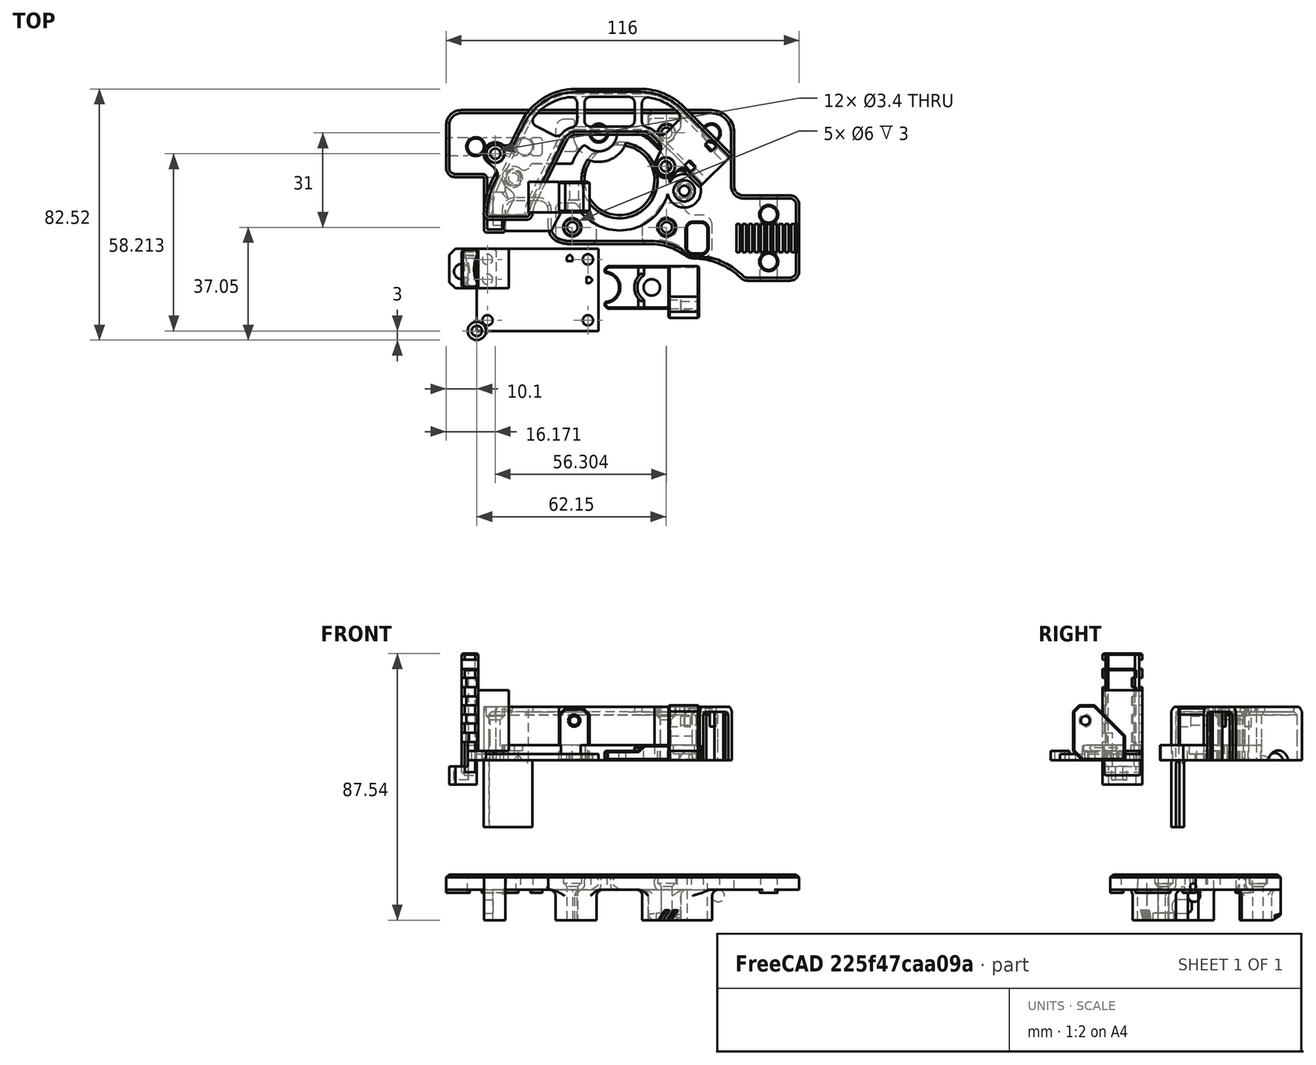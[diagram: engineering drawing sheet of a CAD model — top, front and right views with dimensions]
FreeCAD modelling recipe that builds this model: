
FCSTD DOCUMENT  (FreeCAD 0.19R24291 (Git))
Label: toolhead-pcb-mounter
License: Other
LicenseURL: GPL3
objects: Part::Cylinder×26, Part::Cut×26, Part::Box×24, Part::Chamfer×17, Part::MultiFuse×16, Part::Feature×10, Part::Fillet×6, Part::Extrusion×2, Part::MultiCommon×1
note: 128 computed .brp shape members not serialized (recipe doc carries the construction recipe); baked Part::Feature solids carry a one-line shape summary decoded from their .brp

FEATURE [Part::Box] Box  label="Cube"
  AttacherType = Attacher::AttachEngine3D
  Height = 2
  Length = 40
  Width = 27
FEATURE [Part::Cylinder] Cylinder
  Angle = 360
  AttacherType = Attacher::AttachEngine3D
  Height = 10
  Placement = pos=(3.5,3.5,0) rot=(0,0,1;0rad)
  Radius = 1.7
FEATURE [Part::Cylinder] Cylinder001
  Angle = 360
  AttacherType = Attacher::AttachEngine3D
  Height = 10
  Placement = pos=(3.5,23.5,0) rot=(0,0,1;0rad)
  Radius = 1.7
FEATURE [Part::Cylinder] Cylinder002
  Angle = 360
  AttacherType = Attacher::AttachEngine3D
  Height = 10
  Placement = pos=(36.5,3.5,0) rot=(0,0,1;0rad)
  Radius = 1.7
FEATURE [Part::Cylinder] Cylinder003
  Angle = 360
  AttacherType = Attacher::AttachEngine3D
  Height = 10
  Placement = pos=(36.5,23.5,0) rot=(0,0,1;0rad)
  Radius = 1.7
FEATURE [Part::Cylinder] Cylinder004
  Angle = 360
  AttacherType = Attacher::AttachEngine3D
  Height = 10
  Placement = pos=(3.5,17,0) rot=(0,0,1;0rad)
  Radius = 1.7
FEATURE [Part::MultiFuse] Fusion
  Shapes = -> [Cylinder004,Cylinder,Cylinder001,Cylinder002,Cylinder003]
FEATURE [Part::Cut] Cut
  Base = -> Box
  Tool = -> Fusion
FEATURE [Part::Box] Box001  label="Cube001"
  AttacherType = Attacher::AttachEngine3D
  Height = 10
  Length = 2
  Placement = pos=(29.5,23,0) rot=(0,0,1;0rad)
  Width = 2
FEATURE [Part::Box] Box002  label="Cube002"
  AttacherType = Attacher::AttachEngine3D
  Height = 10
  Length = 2
  Placement = pos=(36,15.7,0) rot=(0,0,1;0rad)
  Width = 2
FEATURE [Part::Chamfer] Chamfer
  Base = -> Box002
  Edges = 2 edges r=0.9: [Edge5,Edge7]
FEATURE [Part::Chamfer] Chamfer001
  Base = -> Box001
  Edges = 2 edges r=0.8: [Edge3,Edge7]
FEATURE [Part::MultiFuse] Fusion001
  Shapes = -> [Chamfer,Chamfer001]
FEATURE [Part::Cut] Cut001  label="pcb"
  Base = -> Cut
  Tool = -> Fusion001
FEATURE [Part::Cylinder] Cylinder005
  Angle = 360
  AttacherType = Attacher::AttachEngine3D
  Height = 3
  Radius = 3
FEATURE [Part::Cylinder] Cylinder006
  Angle = 360
  AttacherType = Attacher::AttachEngine3D
  Height = 3
  Radius = 1.7
FEATURE [Part::Cylinder] Cylinder007
  Angle = 360
  AttacherType = Attacher::AttachEngine3D
  Height = 10
  Radius = 4.75
FEATURE [Part::Cylinder] Cylinder008
  Angle = 360
  AttacherType = Attacher::AttachEngine3D
  Height = 10
  Placement = pos=(15.5,0,0) rot=(0,0,1;0rad)
  Radius = 2.7
FEATURE [Part::Box] Box003  label="Cube003"
  AttacherType = Attacher::AttachEngine3D
  Height = 5
  Length = 22
  Placement = pos=(0,-7,0) rot=(0,0,1;0rad)
  Width = 14
FEATURE [Part::Cut] Cut003
  Base = -> Box003
  Tool = -> Cylinder007
FEATURE [Part::Box] Box004  label="Cube004"
  AttacherType = Attacher::AttachEngine3D
  Height = 18
  Length = 10
  Placement = pos=(21,-10,0) rot=(0,0,1;0rad)
  Width = 17
FEATURE [Part::Cylinder] Cylinder009
  Angle = 360
  AttacherType = Attacher::AttachEngine3D
  Height = 5
  Placement = pos=(15.5,0,0) rot=(0,0,1;0rad)
  Radius = 5.75
FEATURE [Part::Chamfer] Chamfer002
  Base = -> Cut003
  Edges = 2 edges r=1: [Edge4,Edge20]
FEATURE [Part::Box] Box005  label="Cube005"
  AttacherType = Attacher::AttachEngine3D
  Height = 10
  Length = 18
  Placement = pos=(-24,-7,3) rot=(0,0,1;0rad)
  Width = 14
FEATURE [Part::Chamfer] Chamfer006
  Base = -> Box005
  Edges = 1 edges r=2: [Edge8]
  Placement = pos=(19,0,0) rot=(0,0,1;0rad)
FEATURE [Part::Cut] Cut004
  Base = -> Chamfer002
  Tool = -> Chamfer006
FEATURE [Part::Chamfer] Chamfer008
  Base = -> Cut004
  Edges = 21 edges r=0.4: [Edge1,Edge2,Edge3,Edge5,Edge7,Edge8,Edge9,Edge10,Edge11,Edge12,Edge15,Edge16,Edge17,Edge19,Edge20,Edge21,Edge24,Edge25,Edge27,Edge30,Edge31]
FEATURE [Part::Cylinder] Cylinder010
  Angle = 360
  AttacherType = Attacher::AttachEngine3D
  Height = 4
  Placement = pos=(21,0,18) rot=(0,1,0;1.5708rad)
  Radius = 2
FEATURE [Part::Chamfer] Chamfer001002004
  Base = -> Cylinder009
  Edges = 1 edges r=1: [Edge1]
FEATURE [Part::MultiFuse] Fusion002
  Shapes = -> [Chamfer001002004,Chamfer008]
FEATURE [Part::Cut] Cut005
  Base = -> Fusion002
  Tool = -> Cylinder008
FEATURE [Part::Cylinder] Cylinder011
  Angle = 360
  AttacherType = Attacher::AttachEngine3D
  Height = 13
  Placement = pos=(21,0,18) rot=(0,1,0;1.5708rad)
  Radius = 1.45
FEATURE [Part::Cylinder] Cylinder012
  Angle = 360
  AttacherType = Attacher::AttachEngine3D
  Height = 10
  Placement = pos=(3.5,17,0) rot=(0,0,1;0rad)
  Radius = 1.65
FEATURE [Part::Cylinder] Cylinder013
  Angle = 360
  AttacherType = Attacher::AttachEngine3D
  Height = 10
  Placement = pos=(3.5,23.5,0) rot=(0,0,1;0rad)
  Radius = 1.65
FEATURE [Part::Box] Box006  label="Cube006"
  AttacherType = Attacher::AttachEngine3D
  Height = 3
  Length = 6.5
  Placement = pos=(0,14,0) rot=(0,0,1;0rad)
  Width = 13
FEATURE [Part::Box] Box007  label="Cube007"
  AttacherType = Attacher::AttachEngine3D
  Height = 35
  Length = 7
  Placement = pos=(-5,14,-5) rot=(0,0,1;0rad)
  Width = 13
FEATURE [Part::Cylinder] Cylinder014
  Angle = 360
  AttacherType = Attacher::AttachEngine3D
  Height = 48
  Placement = pos=(-12.75,19.5,-6) rot=(0,0,1;0rad)
  Radius = 10
FEATURE [Part::Box] Box008  label="Cube008"
  AttacherType = Attacher::AttachEngine3D
  Height = 10
  Length = 10
  Placement = pos=(0,14,-10) rot=(0,0,1;0rad)
  Width = 13
FEATURE [Part::Box] Box009  label="Cube009"
  AttacherType = Attacher::AttachEngine3D
  Height = 20
  Length = 10
  Placement = pos=(0.5,14,3) rot=(0,0,1;0rad)
  Width = 13
FEATURE [Part::Box] Box010  label="Cube010"
  AttacherType = Attacher::AttachEngine3D
  Height = 43
  Length = 10
  Placement = pos=(0.5,14,-8) rot=(0,0,1;0rad)
  Width = 13
FEATURE [Part::Box] Box011  label="Cube011"
  AttacherType = Attacher::AttachEngine3D
  Height = 3
  Length = 10
  Placement = pos=(-6,13,6) rot=(0,0,1;0rad)
  Width = 2
FEATURE [Part::Box] Box012  label="Cube012"
  AttacherType = Attacher::AttachEngine3D
  Height = 3
  Length = 10
  Placement = pos=(-6,26,6) rot=(0,0,1;0rad)
  Width = 2
FEATURE [Part::MultiFuse] Fusion007
  Shapes = -> [Box011,Box012]
FEATURE [Part::Feature] Fusion007001  label="Fusion008"
  Placement = pos=(0,0,6) rot=(0,0,1;0rad)
  shape: bbox 10 x 15 x 3 mm, 12 faces, 2 solids (baked)
FEATURE [Part::Feature] Fusion007002  label="Fusion009"
  Placement = pos=(0,0,12) rot=(0,0,1;0rad)
  shape: bbox 10 x 15 x 3 mm, 12 faces, 2 solids (baked)
FEATURE [Part::MultiFuse] Fusion007004
  Shapes = -> [Cylinder013,Cylinder012]
FEATURE [Part::Cut] Cut013
  Base = -> Box006
  Tool = -> Fusion007004
FEATURE [Part::Chamfer] Chamfer001002009
  Base = -> Cut013
  Edges = 2 edges r=1: [Edge6,Edge13]
FEATURE [Part::Box] Box013  label="Cube013"
  AttacherType = Attacher::AttachEngine3D
  Height = 2
  Length = 10
  Placement = pos=(0,14,3) rot=(0,0,1;0rad)
  Width = 13
FEATURE [Part::Cut] Cut016  label="washer"
  Base = -> Cylinder005
  Tool = -> Cylinder006
FEATURE [Part::Feature] Fusion007009
  Placement = pos=(0,0,18) rot=(0,0,1;0rad)
  shape: bbox 10 x 15 x 3 mm, 12 faces, 2 solids (baked)
FEATURE [Part::Feature] Cut024001  label="30mm"
  shape: bbox 11.5 x 13 x 40 mm, 108 faces (baked)
FEATURE [Part::Chamfer] Chamfer001002020
  Base = -> Box004
  Edges = 1 edges r=3: [Edge9]
FEATURE [Part::Chamfer] Chamfer001002021
  Base = -> Chamfer001002020
  Edges = 1 edges r=10: [Edge11]
FEATURE [Part::Chamfer] Chamfer001002022
  Base = -> Chamfer001002021
  Edges = 1 edges r=2: [Edge8]
FEATURE [Part::Chamfer] Chamfer001002023
  Base = -> Chamfer001002022
  Edges = 15 edges r=0.4: [Edge1,Edge2,Edge3,Edge4,Edge5,Edge6,Edge7,Edge10,Edge12,Edge14,Edge15,Edge17,Edge18,Edge20,Edge21]
FEATURE [Part::MultiFuse] Fusion007007002
  Placement = pos=(0,-6,-5) rot=(0,0,1;0rad)
  Shapes = -> [Cylinder011,Cylinder010]
FEATURE [Part::Cut] Cut024007
  Base = -> Chamfer001002023
  Tool = -> Fusion007007002
FEATURE [Part::MultiFuse] Fusion007007003
  Placement = pos=(42,14.3,0) rot=(0,0,1;0rad)
  Shapes = -> [Cut024007,Cut005]
FEATURE [Part::Feature] Fusion007007002001  label="Fusion007007004"
  Placement = pos=(25,16,-5) rot=(0,0,1;1.5708rad)
  shape: bbox 4 x 13 x 4 mm, 6 faces (baked)
FEATURE [Part::Feature] Chamfer001001  label="Chamfer001002024"
  Placement = pos=(36,60,0) rot=(0,0,-1;1.5708rad)
  shape: bbox 83.66 x 44.65 x 40.8 mm, 295 faces (baked)
FEATURE [Part::Box] Box014  label="Cube014"
  AttacherType = Attacher::AttachEngine3D
  Height = 17.5
  Length = 10
  Placement = pos=(17,39,0) rot=(0,0,1;0rad)
  Width = 10
FEATURE [Part::Feature] Part__Feature200_cs001
  Placement = pos=(42,52,-10.5) rot=(0,0,-1;1.5708rad)
  shape: bbox 81.47 x 42.81 x 1e-05 mm, 0 faces, 0 solids (baked)
FEATURE [Part::Extrusion] Extrude
  Base = -> Part__Feature200_cs001
  Dir = (0,0,1)
  DirMode = 2
  FaceMakerClass = Part::FaceMakerBullseye
  LengthFwd = 5
  LengthRev = 0
  Solid = true
  Symmetric = false
FEATURE [Part::Box] Box015  label="Cube015"
  AttacherType = Attacher::AttachEngine3D
  Height = 10
  Length = 94
  Placement = pos=(0,55,0) rot=(0,0,1;0rad)
  Width = 20
FEATURE [Part::Cut] Cut024008
  Base = -> Extrude
  Tool = -> Box015
FEATURE [Part::Fillet] Fillet
  Base = -> Cut024008
  Edges = 1 edges r=1: [Edge48]
FEATURE [Part::Fillet] Fillet001
  Base = -> Fillet
  Edges = 1 edges r=1: [Edge54]
FEATURE [Part::Box] Box017  label="Cube017"
  AttacherType = Attacher::AttachEngine3D
  Height = 10
  Length = 24
  Placement = pos=(72,38,0) rot=(0,0,1;0rad)
  Width = 20
FEATURE [Part::Cut] Cut024009
  Base = -> Fillet001
  Tool = -> Box017
FEATURE [Part::Fillet] Fillet002
  Base = -> Cut024009
  Edges = 1 edges r=1: [Edge12]
FEATURE [Part::Fillet] Fillet003
  Base = -> Fillet002
  Edges = 1 edges r=5: [Edge12]
FEATURE [Part::Box] Box018  label="Cube018"
  AttacherType = Attacher::AttachEngine3D
  Height = 10
  Length = 30
  Placement = pos=(0,22.87,0) rot=(0,0,1;0rad)
  Width = 10
FEATURE [Part::Box] Box019  label="Cube019"
  AttacherType = Attacher::AttachEngine3D
  Height = 17
  Length = 10
  Placement = pos=(20,37,0) rot=(0,0,1;0rad)
  Width = 10
FEATURE [Part::Chamfer] Chamfer001002024  label="Chamfer001002025"
  Base = -> Box019
  Edges = 2 edges r=2: [Edge2,Edge6]
FEATURE [Part::Chamfer] Chamfer001002025  label="Chamfer001002026"
  Base = -> Chamfer001002024
  Edges = 12 edges r=0.4: [Edge1,Edge4,Edge5,Edge6,Edge7,Edge8,Edge9,Edge11,Edge12,Edge14,Edge15,Edge16]
FEATURE [Part::Cut] Cut024011
  Base = -> Chamfer001002025
  Placement = pos=(7,2,0) rot=(0,0,1;0rad)
  Tool = -> Fusion007007002001
FEATURE [Part::Cylinder] Cylinder015
  Angle = 360
  AttacherType = Attacher::AttachEngine3D
  Height = 3
  Placement = pos=(12.06,50.21,0) rot=(0,0,1;0rad)
  Radius = 3.5
FEATURE [Part::Cylinder] Cylinder016
  Angle = 360
  AttacherType = Attacher::AttachEngine3D
  Height = 3
  Placement = pos=(68.15,46.04,2) rot=(0,0,1;0rad)
  Radius = 3.5
FEATURE [Part::Cylinder] Cylinder017
  Angle = 360
  AttacherType = Attacher::AttachEngine3D
  Height = 7
  Placement = pos=(68.15,46.04,0) rot=(0,0,1;0rad)
  Radius = 1.65
FEATURE [Part::Cylinder] Cylinder018
  Angle = 360
  AttacherType = Attacher::AttachEngine3D
  Height = 7
  Placement = pos=(12.06,50.21,0) rot=(0,0,1;0rad)
  Radius = 1.65
FEATURE [Part::MultiFuse] Fusion007007002004
  Shapes = -> [Cylinder018,Cylinder017]
FEATURE [Part::Feature] Part__Feature176  label="COMPOUND"
  Placement = pos=(62.92,52.05,-85.85) rot=(0,0,-1;1.5708rad)
  shape: bbox 116 x 59.91 x 16.88 mm, 381 faces (baked)
FEATURE [Part::Cylinder] Cylinder019
  Angle = 360
  AttacherType = Attacher::AttachEngine3D
  Height = 5
  Placement = pos=(46.89,49.53,0) rot=(0,0,1;0rad)
  Radius = 12.5
FEATURE [Part::Cylinder] Cylinder020
  Angle = 360
  AttacherType = Attacher::AttachEngine3D
  Height = 5
  Placement = pos=(46.89,49.53,0) rot=(0,0,1;0rad)
  Radius = 16.5
FEATURE [Part::Cut] Cut024013
  Base = -> Cylinder020
  Tool = -> Cylinder019
FEATURE [Part::Cylinder] Cylinder021
  Angle = 360
  AttacherType = Attacher::AttachEngine3D
  Height = 5
  Placement = pos=(40.09,65.03,0) rot=(0,0,1;0rad)
  Radius = 6
FEATURE [Part::Cylinder] Cylinder022
  Angle = 360
  AttacherType = Attacher::AttachEngine3D
  Height = 5
  Placement = pos=(46.89,49.53,0) rot=(0,0,1;0rad)
  Radius = 16.5
FEATURE [Part::Cylinder] Cylinder023
  Angle = 360
  AttacherType = Attacher::AttachEngine3D
  Height = 5
  Placement = pos=(40.09,65.03,0) rot=(0,0,1;0rad)
  Radius = 9.5
FEATURE [Part::MultiCommon] Common
  Shapes = -> [Cylinder022,Cylinder023]
FEATURE [Part::MultiFuse] Fusion007007002006
  Shapes = -> [Cut024013,Common]
FEATURE [Part::Cut] Cut024014
  Base = -> Fusion007007002006
  Tool = -> Cylinder021
FEATURE [Part::Fillet] Fillet005
  Base = -> Cut024014
  Edges = 2 edges r=1: [Edge15,Edge22]
FEATURE [Part::Cut] Cut024015
  Base = -> Fillet003
  Tool = -> Box018
FEATURE [Part::Box] Box020  label="Cube020"
  AttacherType = Attacher::AttachEngine3D
  Height = 10
  Length = 16
  Placement = pos=(62,37,0) rot=(0,0,1;0rad)
  Width = 22
FEATURE [Part::Cut] Cut024016
  Base = -> Cut024015
  Tool = -> Box020
FEATURE [Part::Cylinder] Cylinder024
  Angle = 360
  AttacherType = Attacher::AttachEngine3D
  Height = 5
  Placement = pos=(68.15,46.04,0) rot=(0,0,1;0rad)
  Radius = 5.5
FEATURE [Part::MultiFuse] Fusion007007002007
  Shapes = -> [Fillet005,Cylinder024]
FEATURE [Part::Cut] Cut024017
  Base = -> Fusion007007002007
  Tool = -> Cylinder016
FEATURE [Part::MultiFuse] Fusion007007002008
  Shapes = -> [Cut024016,Cut024011,Cut024017]
FEATURE [Part::MultiFuse] Fusion007007002009
  Shapes = -> [Fusion007007002008,Cylinder015]
FEATURE [Part::Cut] Cut024018
  Base = -> Fusion007007002009
  Tool = -> Fusion007007002004
FEATURE [Part::Fillet] Fillet006
  Base = -> Cut024018
  Edges = 2 edges r=1: [Edge47,Edge51]
FEATURE [Part::Box] Box021  label="Cube021"
  AttacherType = Attacher::AttachEngine3D
  Height = 43
  Length = 10
  Placement = pos=(-14,14,-8) rot=(0,0,1;0rad)
  Width = 13
FEATURE [Part::Box] Box022  label="Cube022"
  AttacherType = Attacher::AttachEngine3D
  Height = 16
  Length = 10
  Placement = pos=(-13,10.5,-7) rot=(0,0,1;0rad)
  Width = 10
FEATURE [Part::MultiFuse] Fusion007010
  Shapes = -> [Fusion007,Fusion007001,Fusion007002,Fusion007009]
FEATURE [Part::Feature] Fusion007010001
  Placement = pos=(0,-2,0) rot=(0,0,1;0rad)
  shape: bbox 10 x 15 x 21 mm, 48 faces, 8 solids (baked)
FEATURE [Part::MultiFuse] Fusion007007002010
  Shapes = -> [Fusion007010001,Fusion007010]
FEATURE [Part::Box] Box023  label="Cube023"
  AttacherType = Attacher::AttachEngine3D
  Height = 35
  Length = 7
  Placement = pos=(-5,25,5) rot=(0,0,1;0rad)
  Width = 11
FEATURE [Part::Cut] Cut024019
  Base = -> Box007
  Tool = -> Cylinder014
FEATURE [Part::Cut] Cut024020
  Base = -> Cut024019
  Tool = -> Box021
FEATURE [Part::Cut] Cut024021
  Base = -> Cut024020
  Tool = -> Box022
FEATURE [Part::Cut] Cut024022
  Base = -> Cut024021
  Tool = -> Box010
FEATURE [Part::Cut] Cut024023
  Base = -> Cut024022
  Tool = -> Box013
FEATURE [Part::Cut] Cut024024
  Base = -> Cut024023
  Tool = -> Box008
FEATURE [Part::Cut] Cut024025
  Base = -> Cut024024
  Tool = -> Box023
FEATURE [Part::MultiFuse] Fusion007007002011
  Shapes = -> [Cut024025,Chamfer001002009]
FEATURE [Part::Cut] Cut024026
  Base = -> Fusion007007002011
  Tool = -> Fusion007007002010
FEATURE [Part::Chamfer] Chamfer001002026  label="Chamfer001002027"
  Base = -> Cut024026
  Edges = 7 edges r=0.4: [Edge1,Edge2,Edge3,Edge4,Edge5,Edge6,Edge7]
FEATURE [Part::Chamfer] Chamfer001002027  label="Chamfer001002028"
  Base = -> Chamfer001002026
  Edges = 16 edges r=0.4: [Edge29,Edge33,Edge37,Edge41,Edge47,Edge51,Edge55,Edge64,Edge68,Edge72,Edge76,Edge82,Edge86,Edge90,Edge94,Edge139]
FEATURE [Part::Chamfer] Chamfer001002028  label="Chamfer001002029"
  Base = -> Chamfer001002027
  Edges = 1 edges r=1: [Edge40]
FEATURE [Part::Feature] Chamfer001002028_cs
  shape: bbox 4 x 13 x 3e-07 mm, 0 faces, 0 solids (baked)
FEATURE [Part::Extrusion] Extrude001
  Base = -> Chamfer001002028_cs
  Dir = (0,0,1)
  DirMode = 2
  FaceMakerClass = Part::FaceMakerBullseye
  LengthFwd = 4
  LengthRev = 0
  Placement = pos=(0,0,-5.5) rot=(0,0,1;0rad)
  Solid = true
  Symmetric = false
FEATURE [Part::Box] Box024  label="Cube024"
  AttacherType = Attacher::AttachEngine3D
  Height = 6
  Length = 9
  Placement = pos=(-9,14,-8) rot=(0,0,1;0rad)
  Width = 13
FEATURE [Part::Cylinder] Cylinder025
  Angle = 360
  AttacherType = Attacher::AttachEngine3D
  Height = 10
  Placement = pos=(-5,19.5,-6.5) rot=(0,0,1;0rad)
  Radius = 2.5
FEATURE [Part::Chamfer] Chamfer001002029  label="Chamfer001002030"
  Base = -> Box024
  Edges = 2 edges r=2: [Edge1,Edge3]
FEATURE [Part::Cut] Cut024027
  Base = -> Chamfer001002029
  Tool = -> Cylinder025
FEATURE [Part::MultiFuse] Fusion007007002012
  Shapes = -> [Cut024027,Extrude001,Chamfer001002028]
